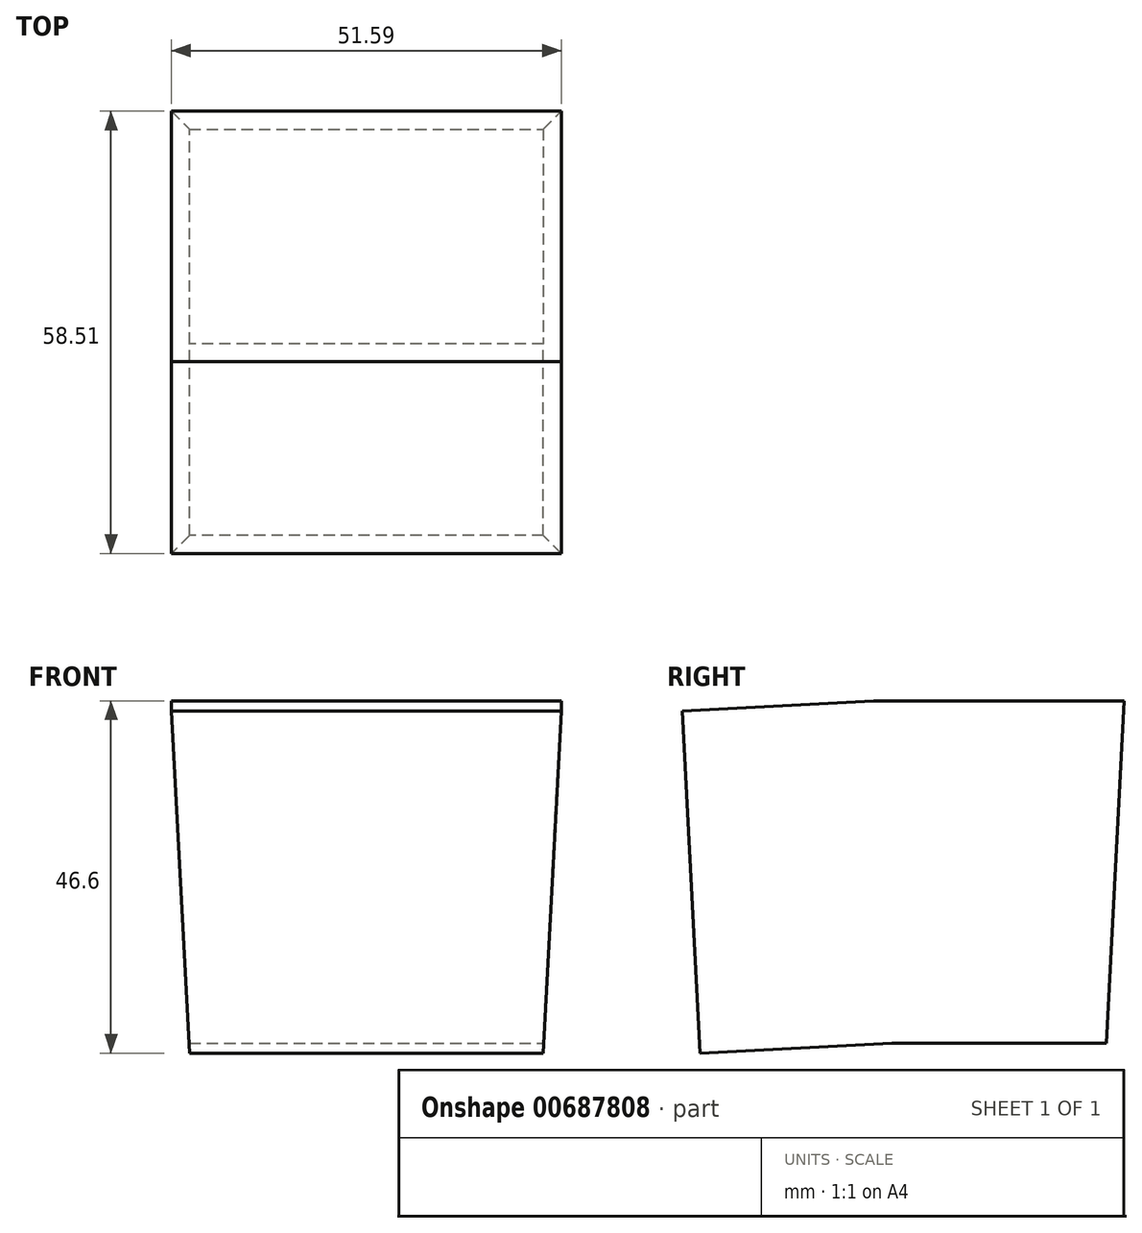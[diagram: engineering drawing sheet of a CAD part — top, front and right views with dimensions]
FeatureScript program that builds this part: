
annotation { "Feature Type Name" : "Feature", "Feature Type Description" : "" }
export const myFeature = defineFeature(function(context is Context, id is Id, definition is map)
    precondition{}
    {
        {
            var Q0;
            Q0=qCreatedBy(makeId("Top.planeOp"),FACE);
            var sketch = newSketch(context, id + "F0", { "sketchPlane" : qUnion([Q0])});
            skLineSegment(sketch, "E0.bottom", {"start": v(0, 0) * mm, "end": v(46.85, 0) * mm});
            skLineSegment(sketch, "E0.top", {"start": v(0, 28.4) * mm, "end": v(46.85, 28.4) * mm});
            skLineSegment(sketch, "E0.left", {"start": v(0, 0) * mm, "end": v(0, 28.4) * mm});
            skLineSegment(sketch, "E0.right", {"start": v(46.85, 0) * mm, "end": v(46.85, 28.4) * mm});
            skSolve(sketch);
        }
        {
            var Q0;
            Q0=makeQuery(id+"F0.imprint","IMPRINT",FACE,{"disambiguationData":[TD([[makeQuery(id+"F0.imprint","IMPRINT",EDGE,{"derivedFrom":sQuery(id+"F0.wireOp",EDGE,"E0.bottom")}),1.0]])]});
            extrude(context, id + "F1", {"entities" : qUnion([Q0]), "depth" : 45.27 * mm, "offsetDistance" : 25.4 * mm, "hasDraft" : true, "draftAngle" : 3 * degree});
        }
        {
            var Q0;
            Q0=makeQuery(id+"F1.opExtrude","SWEPT_FACE",FACE,{"disambiguationData":[OSD([sQuery(id+"F0.wireOp",EDGE,"E0.bottom")])]});
            extrude(context, id + "F2", {"entities" : qUnion([Q0]), "operationType" : NewBodyOperationType.ADD, "depth" : 25.4 * mm, "offsetDistance" : 25.4 * mm});
        }
    });
